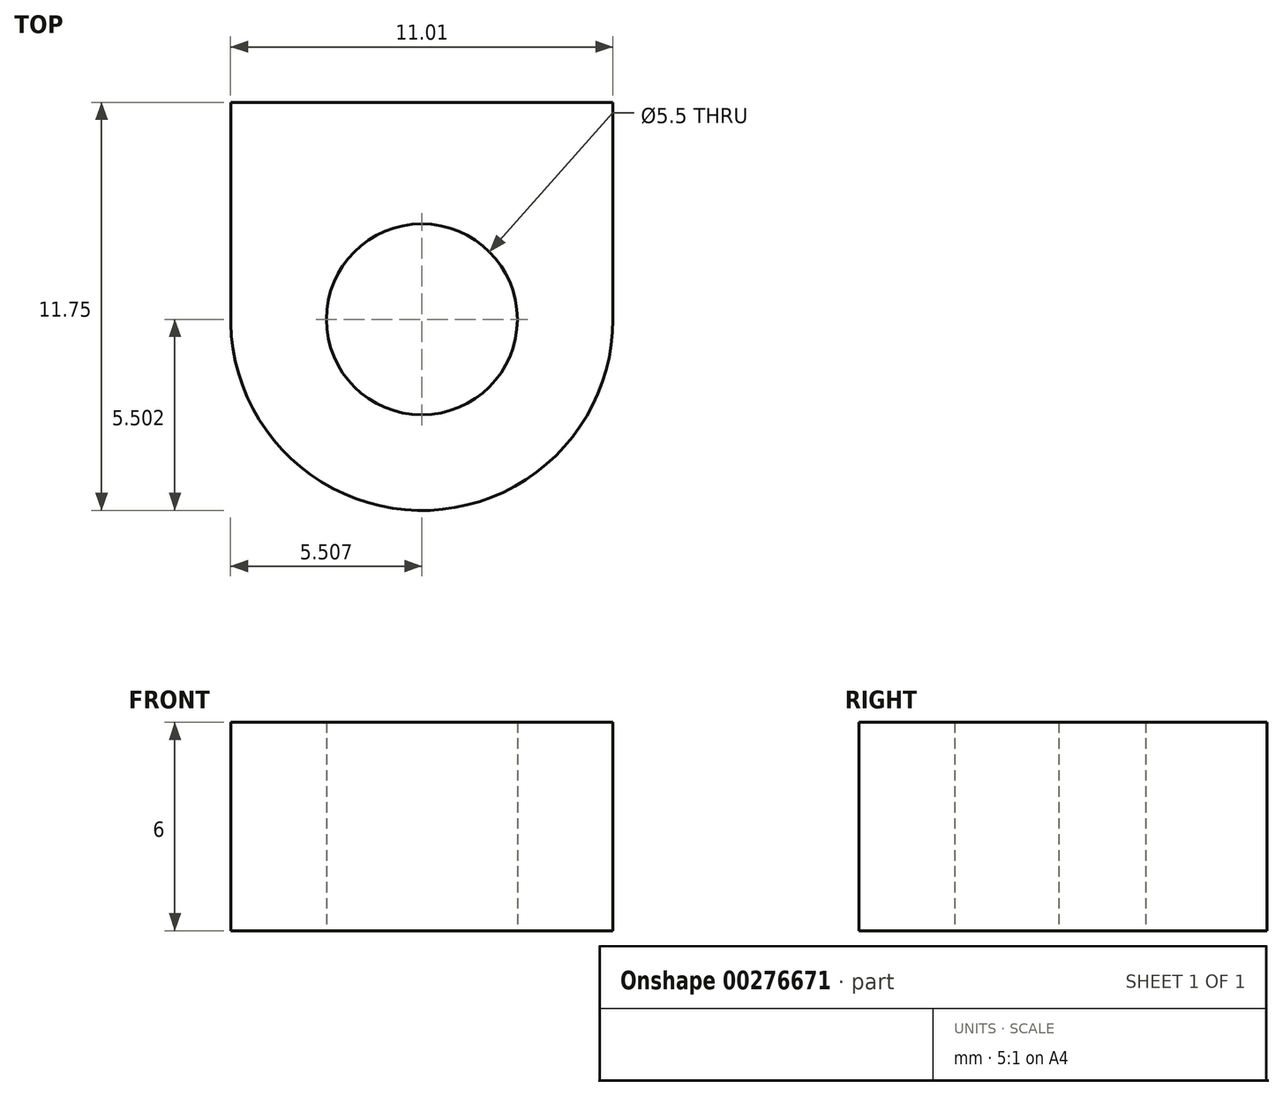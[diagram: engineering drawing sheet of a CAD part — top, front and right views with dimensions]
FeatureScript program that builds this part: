
annotation { "Feature Type Name" : "Feature", "Feature Type Description" : "" }
export const myFeature = defineFeature(function(context is Context, id is Id, definition is map)
    precondition{}
    {
        {
            var Q0;
            Q0=qCreatedBy(makeId("Top.planeOp"),FACE);
            var sketch = newSketch(context, id + "F0", { "sketchPlane" : qUnion([Q0])});
            skLineSegment(sketch, "E0.bottom", {"start": v(-5, -2.48) * mm, "end": v(6, -2.48) * mm});
            skLineSegment(sketch, "E0.left", {"start": v(-5, -2.48) * mm, "end": v(-5, -8.48) * mm});
            skLineSegment(sketch, "E0.right", {"start": v(6, -2.48) * mm, "end": v(6, -8.73) * mm});
            skArc(sketch, "E1", {"start": v(-5, -8.48) * mm, "mid": v(0.37, -14.23) * mm, "end": v(6, -8.73) * mm});
            skCircle(sketch, "E2", {"center": v(0.5, -8.73) * mm, "radius": 2.75 * mm});
            skSolve(sketch);
        }
        {
            var Q0;
            Q0 = qSketchRegion(id + "F0", true);
            extrude(context, id + "F1", {"entities" : qUnion([Q0]), "depth" : 6 * mm});
        }
    });
